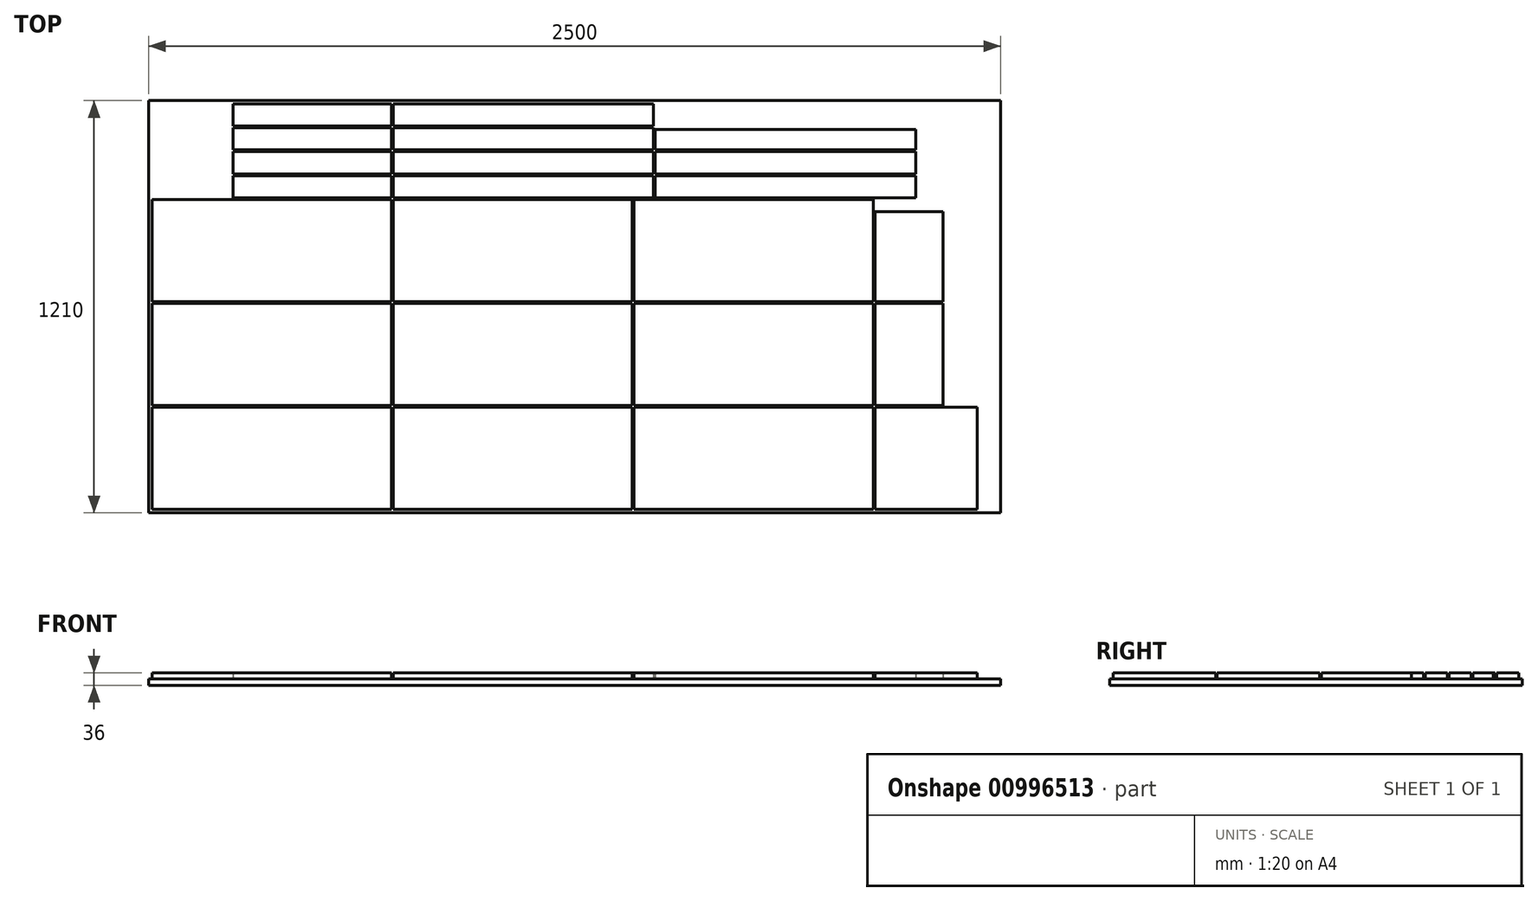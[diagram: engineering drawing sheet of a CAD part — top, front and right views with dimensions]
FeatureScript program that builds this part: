
annotation { "Feature Type Name" : "Feature", "Feature Type Description" : "" }
export const myFeature = defineFeature(function(context is Context, id is Id, definition is map)
    precondition{}
    {
        {
            var Q0;
            Q0=qCreatedBy(makeId("Top.planeOp"),FACE);
            var sketch = newSketch(context, id + "F0", { "sketchPlane" : qUnion([Q0])});
            skLineSegment(sketch, "E0.bottom", {"start": v(0, 0) * mm, "end": v(2500, 0) * mm});
            skLineSegment(sketch, "E0.top", {"start": v(0, 1210) * mm, "end": v(2500, 1210) * mm});
            skLineSegment(sketch, "E0.left", {"start": v(0, 0) * mm, "end": v(0, 1210) * mm});
            skLineSegment(sketch, "E0.right", {"start": v(2500, 0) * mm, "end": v(2500, 1210) * mm});
            skSolve(sketch);
        }
        {
            var Q0;
            Q0=makeQuery(id+"F0.imprint","IMPRINT",FACE,{"disambiguationData":[TD([[makeQuery(id+"F0.imprint","IMPRINT",EDGE,{"derivedFrom":sQuery(id+"F0.wireOp",EDGE,"E0.bottom")}),1.0]])]});
            extrude(context, id + "F1", {"entities" : qUnion([Q0]), "depth" : 18 * mm, "offsetDistance" : 25 * mm});
        }
        {
            var Q0;
            Q0=makeQuery(id+"F1.opExtrude","CAP_FACE",FACE,{"disambiguationData":[OSD([sQuery(id+"F0.wireOp",EDGE,"E0.bottom"),sQuery(id+"F0.wireOp",EDGE,"E0.top"),sQuery(id+"F0.wireOp",EDGE,"E0.left"),sQuery(id+"F0.wireOp",EDGE,"E0.right")])],"isStart":false});
            var sketch = newSketch(context, id + "F2", { "sketchPlane" : qUnion([Q0])});
            skLineSegment(sketch, "E1.bottom", {"start": v(10, 10) * mm, "end": v(712, 10) * mm});
            skLineSegment(sketch, "E1.top", {"start": v(10, 310) * mm, "end": v(712, 310) * mm});
            skLineSegment(sketch, "E1.left", {"start": v(10, 10) * mm, "end": v(10, 310) * mm});
            skLineSegment(sketch, "E1.right", {"start": v(712, 10) * mm, "end": v(712, 310) * mm});
            skLineSegment(sketch, "E2.bottom", {"start": v(717, 10) * mm, "end": v(1419, 10) * mm});
            skLineSegment(sketch, "E2.top", {"start": v(717, 310) * mm, "end": v(1419, 310) * mm});
            skLineSegment(sketch, "E2.left", {"start": v(717, 10) * mm, "end": v(717, 310) * mm});
            skLineSegment(sketch, "E2.right", {"start": v(1419, 10) * mm, "end": v(1419, 310) * mm});
            skLineSegment(sketch, "E3.bottom", {"start": v(10, 315) * mm, "end": v(712, 315) * mm});
            skLineSegment(sketch, "E3.top", {"start": v(10, 615) * mm, "end": v(712, 615) * mm});
            skLineSegment(sketch, "E3.left", {"start": v(10, 315) * mm, "end": v(10, 615) * mm});
            skLineSegment(sketch, "E3.right", {"start": v(712, 315) * mm, "end": v(712, 615) * mm});
            skLineSegment(sketch, "E4.bottom", {"start": v(717, 615) * mm, "end": v(1419, 615) * mm});
            skLineSegment(sketch, "E4.top", {"start": v(717, 315) * mm, "end": v(1419, 315) * mm});
            skLineSegment(sketch, "E4.left", {"start": v(717, 615) * mm, "end": v(717, 315) * mm});
            skLineSegment(sketch, "E4.right", {"start": v(1419, 615) * mm, "end": v(1419, 315) * mm});
            skLineSegment(sketch, "E5.bottom", {"start": v(10, 620) * mm, "end": v(712, 620) * mm});
            skLineSegment(sketch, "E5.top", {"start": v(10, 920) * mm, "end": v(712, 920) * mm});
            skLineSegment(sketch, "E5.left", {"start": v(10, 620) * mm, "end": v(10, 920) * mm});
            skLineSegment(sketch, "E5.right", {"start": v(712, 620) * mm, "end": v(712, 920) * mm});
            skLineSegment(sketch, "E6.bottom", {"start": v(717, 920) * mm, "end": v(1419, 920) * mm});
            skLineSegment(sketch, "E6.top", {"start": v(717, 620) * mm, "end": v(1419, 620) * mm});
            skLineSegment(sketch, "E6.left", {"start": v(717, 920) * mm, "end": v(717, 620) * mm});
            skLineSegment(sketch, "E6.right", {"start": v(1419, 920) * mm, "end": v(1419, 620) * mm});
            skLineSegment(sketch, "E7.bottom", {"start": v(1424, 310) * mm, "end": v(2126, 310) * mm});
            skLineSegment(sketch, "E7.top", {"start": v(1424, 10) * mm, "end": v(2126, 10) * mm});
            skLineSegment(sketch, "E7.left", {"start": v(1424, 310) * mm, "end": v(1424, 10) * mm});
            skLineSegment(sketch, "E7.right", {"start": v(2126, 310) * mm, "end": v(2126, 10) * mm});
            skLineSegment(sketch, "E8.bottom", {"start": v(1424, 615) * mm, "end": v(2126, 615) * mm});
            skLineSegment(sketch, "E8.top", {"start": v(1424, 315) * mm, "end": v(2126, 315) * mm});
            skLineSegment(sketch, "E8.left", {"start": v(1424, 615) * mm, "end": v(1424, 315) * mm});
            skLineSegment(sketch, "E8.right", {"start": v(2126, 615) * mm, "end": v(2126, 315) * mm});
            skLineSegment(sketch, "E9.bottom", {"start": v(1424, 920) * mm, "end": v(2126, 920) * mm});
            skLineSegment(sketch, "E9.top", {"start": v(1424, 620) * mm, "end": v(2126, 620) * mm});
            skLineSegment(sketch, "E9.left", {"start": v(1424, 920) * mm, "end": v(1424, 620) * mm});
            skLineSegment(sketch, "E9.right", {"start": v(2126, 920) * mm, "end": v(2126, 620) * mm});
            skLineSegment(sketch, "E10.bottom", {"start": v(2131, 310) * mm, "end": v(2431, 310) * mm});
            skLineSegment(sketch, "E10.top", {"start": v(2131, 10) * mm, "end": v(2431, 10) * mm});
            skLineSegment(sketch, "E10.left", {"start": v(2131, 310) * mm, "end": v(2131, 10) * mm});
            skLineSegment(sketch, "E10.right", {"start": v(2431, 310) * mm, "end": v(2431, 10) * mm});
            skLineSegment(sketch, "E11.bottom", {"start": v(712, 925) * mm, "end": v(248, 925) * mm});
            skLineSegment(sketch, "E11.top", {"start": v(712, 990) * mm, "end": v(248, 990) * mm});
            skLineSegment(sketch, "E11.left", {"start": v(712, 925) * mm, "end": v(712, 990) * mm});
            skLineSegment(sketch, "E11.right", {"start": v(248, 925) * mm, "end": v(248, 990) * mm});
            skLineSegment(sketch, "E12.bottom", {"start": v(248, 1060) * mm, "end": v(712, 1060) * mm});
            skLineSegment(sketch, "E12.top", {"start": v(248, 995) * mm, "end": v(712, 995) * mm});
            skLineSegment(sketch, "E12.left", {"start": v(248, 1060) * mm, "end": v(248, 995) * mm});
            skLineSegment(sketch, "E12.right", {"start": v(712, 1060) * mm, "end": v(712, 995) * mm});
            skLineSegment(sketch, "E13.bottom", {"start": v(248, 1065) * mm, "end": v(712, 1065) * mm});
            skLineSegment(sketch, "E13.top", {"start": v(248, 1130) * mm, "end": v(712, 1130) * mm});
            skLineSegment(sketch, "E13.left", {"start": v(248, 1065) * mm, "end": v(248, 1130) * mm});
            skLineSegment(sketch, "E13.right", {"start": v(712, 1065) * mm, "end": v(712, 1130) * mm});
            skLineSegment(sketch, "E14.bottom", {"start": v(248, 1135) * mm, "end": v(712, 1135) * mm});
            skLineSegment(sketch, "E14.top", {"start": v(248, 1200) * mm, "end": v(712, 1200) * mm});
            skLineSegment(sketch, "E14.left", {"start": v(248, 1135) * mm, "end": v(248, 1200) * mm});
            skLineSegment(sketch, "E14.right", {"start": v(712, 1135) * mm, "end": v(712, 1200) * mm});
            skLineSegment(sketch, "E15.bottom", {"start": v(2131, 315) * mm, "end": v(2331, 315) * mm});
            skLineSegment(sketch, "E15.top", {"start": v(2131, 615) * mm, "end": v(2331, 615) * mm});
            skLineSegment(sketch, "E15.left", {"start": v(2131, 315) * mm, "end": v(2131, 615) * mm});
            skLineSegment(sketch, "E15.right", {"start": v(2331, 315) * mm, "end": v(2331, 615) * mm});
            skLineSegment(sketch, "E16.bottom", {"start": v(2131, 620) * mm, "end": v(2331, 620) * mm});
            skLineSegment(sketch, "E16.top", {"start": v(2131, 884) * mm, "end": v(2331, 884) * mm});
            skLineSegment(sketch, "E16.left", {"start": v(2131, 620) * mm, "end": v(2131, 884) * mm});
            skLineSegment(sketch, "E16.right", {"start": v(2331, 620) * mm, "end": v(2331, 884) * mm});
            skLineSegment(sketch, "E17.bottom", {"start": v(717, 925) * mm, "end": v(1481, 925) * mm});
            skLineSegment(sketch, "E17.top", {"start": v(717, 990) * mm, "end": v(1481, 990) * mm});
            skLineSegment(sketch, "E17.left", {"start": v(717, 925) * mm, "end": v(717, 990) * mm});
            skLineSegment(sketch, "E17.right", {"start": v(1481, 925) * mm, "end": v(1481, 990) * mm});
            skLineSegment(sketch, "E18.bottom", {"start": v(717, 995) * mm, "end": v(1481, 995) * mm});
            skLineSegment(sketch, "E18.top", {"start": v(717, 1060) * mm, "end": v(1481, 1060) * mm});
            skLineSegment(sketch, "E18.left", {"start": v(717, 995) * mm, "end": v(717, 1060) * mm});
            skLineSegment(sketch, "E18.right", {"start": v(1481, 995) * mm, "end": v(1481, 1060) * mm});
            skLineSegment(sketch, "E19.bottom", {"start": v(717, 1065) * mm, "end": v(1481, 1065) * mm});
            skLineSegment(sketch, "E19.top", {"start": v(717, 1130) * mm, "end": v(1481, 1130) * mm});
            skLineSegment(sketch, "E19.left", {"start": v(717, 1065) * mm, "end": v(717, 1130) * mm});
            skLineSegment(sketch, "E19.right", {"start": v(1481, 1065) * mm, "end": v(1481, 1130) * mm});
            skLineSegment(sketch, "E20.bottom", {"start": v(717, 1135) * mm, "end": v(1481, 1135) * mm});
            skLineSegment(sketch, "E20.top", {"start": v(717, 1200) * mm, "end": v(1481, 1200) * mm});
            skLineSegment(sketch, "E20.left", {"start": v(717, 1135) * mm, "end": v(717, 1200) * mm});
            skLineSegment(sketch, "E20.right", {"start": v(1481, 1135) * mm, "end": v(1481, 1200) * mm});
            skLineSegment(sketch, "E21.bottom", {"start": v(1486, 925) * mm, "end": v(2250, 925) * mm});
            skLineSegment(sketch, "E21.top", {"start": v(1486, 990) * mm, "end": v(2250, 990) * mm});
            skLineSegment(sketch, "E21.left", {"start": v(1486, 925) * mm, "end": v(1486, 990) * mm});
            skLineSegment(sketch, "E21.right", {"start": v(2250, 925) * mm, "end": v(2250, 990) * mm});
            skLineSegment(sketch, "E22.bottom", {"start": v(1486, 1060) * mm, "end": v(2250, 1060) * mm});
            skLineSegment(sketch, "E22.top", {"start": v(1486, 995) * mm, "end": v(2250, 995) * mm});
            skLineSegment(sketch, "E22.left", {"start": v(1486, 1060) * mm, "end": v(1486, 995) * mm});
            skLineSegment(sketch, "E22.right", {"start": v(2250, 1060) * mm, "end": v(2250, 995) * mm});
            skLineSegment(sketch, "E23.bottom", {"start": v(1486, 1125) * mm, "end": v(2250, 1125) * mm});
            skLineSegment(sketch, "E23.top", {"start": v(1486, 1065) * mm, "end": v(2250, 1065) * mm});
            skLineSegment(sketch, "E23.left", {"start": v(1486, 1065) * mm, "end": v(1486, 1125) * mm});
            skLineSegment(sketch, "E23.right", {"start": v(2250, 1065) * mm, "end": v(2250, 1125) * mm});
            skLineSegment(sketch, "E24.bottom", {"start": v(0, 1210) * mm, "end": v(2500, 1210) * mm});
            skLineSegment(sketch, "E24.top", {"start": v(0, 0) * mm, "end": v(2500, 0) * mm});
            skLineSegment(sketch, "E24.left", {"start": v(0, 1210) * mm, "end": v(0, 0) * mm});
            skLineSegment(sketch, "E24.right", {"start": v(2500, 1210) * mm, "end": v(2500, 0) * mm});
            skSolve(sketch);
        }
        {
            var Q0;
            Q0=makeQuery(id+"F2.imprint","IMPRINT",FACE,{"disambiguationData":[TD([[makeQuery(id+"F2.imprint","IMPRINT",EDGE,{"derivedFrom":sQuery(id+"F2.wireOp",EDGE,"E1.bottom")}),1.0]])]});
            var Q1;
            Q1=makeQuery(id+"F2.imprint","IMPRINT",FACE,{"disambiguationData":[TD([[makeQuery(id+"F2.imprint","IMPRINT",EDGE,{"derivedFrom":sQuery(id+"F2.wireOp",EDGE,"E3.bottom")}),1.0]])]});
            var Q2;
            Q2=makeQuery(id+"F2.imprint","IMPRINT",FACE,{"disambiguationData":[TD([[makeQuery(id+"F2.imprint","IMPRINT",EDGE,{"derivedFrom":sQuery(id+"F2.wireOp",EDGE,"E5.bottom")}),1.0]])]});
            var Q3;
            Q3=makeQuery(id+"F2.imprint","IMPRINT",FACE,{"disambiguationData":[TD([[makeQuery(id+"F2.imprint","IMPRINT",EDGE,{"derivedFrom":sQuery(id+"F2.wireOp",EDGE,"E2.bottom")}),1.0]])]});
            var Q4;
            Q4=makeQuery(id+"F2.imprint","IMPRINT",FACE,{"disambiguationData":[TD([[makeQuery(id+"F2.imprint","IMPRINT",EDGE,{"derivedFrom":sQuery(id+"F2.wireOp",EDGE,"E4.bottom")}),-1.0]])]});
            var Q5;
            Q5=makeQuery(id+"F2.imprint","IMPRINT",FACE,{"disambiguationData":[TD([[makeQuery(id+"F2.imprint","IMPRINT",EDGE,{"derivedFrom":sQuery(id+"F2.wireOp",EDGE,"E6.bottom")}),-1.0]])]});
            var Q6;
            Q6=makeQuery(id+"F2.imprint","IMPRINT",FACE,{"disambiguationData":[TD([[makeQuery(id+"F2.imprint","IMPRINT",EDGE,{"derivedFrom":sQuery(id+"F2.wireOp",EDGE,"E11.bottom")}),-1.0]])]});
            var Q7;
            Q7=makeQuery(id+"F2.imprint","IMPRINT",FACE,{"disambiguationData":[TD([[makeQuery(id+"F2.imprint","IMPRINT",EDGE,{"derivedFrom":sQuery(id+"F2.wireOp",EDGE,"E12.bottom")}),-1.0]])]});
            var Q8;
            Q8=makeQuery(id+"F2.imprint","IMPRINT",FACE,{"disambiguationData":[TD([[makeQuery(id+"F2.imprint","IMPRINT",EDGE,{"derivedFrom":sQuery(id+"F2.wireOp",EDGE,"E13.bottom")}),1.0]])]});
            var Q9;
            Q9=makeQuery(id+"F2.imprint","IMPRINT",FACE,{"disambiguationData":[TD([[makeQuery(id+"F2.imprint","IMPRINT",EDGE,{"derivedFrom":sQuery(id+"F2.wireOp",EDGE,"E14.bottom")}),1.0]])]});
            var Q10;
            Q10=makeQuery(id+"F2.imprint","IMPRINT",FACE,{"disambiguationData":[TD([[makeQuery(id+"F2.imprint","IMPRINT",EDGE,{"derivedFrom":sQuery(id+"F2.wireOp",EDGE,"E20.bottom")}),1.0]])]});
            var Q11;
            Q11=makeQuery(id+"F2.imprint","IMPRINT",FACE,{"disambiguationData":[TD([[makeQuery(id+"F2.imprint","IMPRINT",EDGE,{"derivedFrom":sQuery(id+"F2.wireOp",EDGE,"E19.bottom")}),1.0]])]});
            var Q12;
            Q12=makeQuery(id+"F2.imprint","IMPRINT",FACE,{"disambiguationData":[TD([[makeQuery(id+"F2.imprint","IMPRINT",EDGE,{"derivedFrom":sQuery(id+"F2.wireOp",EDGE,"E18.bottom")}),1.0]])]});
            var Q13;
            Q13=makeQuery(id+"F2.imprint","IMPRINT",FACE,{"disambiguationData":[TD([[makeQuery(id+"F2.imprint","IMPRINT",EDGE,{"derivedFrom":sQuery(id+"F2.wireOp",EDGE,"E17.bottom")}),1.0]])]});
            var Q14;
            Q14=makeQuery(id+"F2.imprint","IMPRINT",FACE,{"disambiguationData":[TD([[makeQuery(id+"F2.imprint","IMPRINT",EDGE,{"derivedFrom":sQuery(id+"F2.wireOp",EDGE,"E7.bottom")}),-1.0]])]});
            var Q15;
            Q15=makeQuery(id+"F2.imprint","IMPRINT",FACE,{"disambiguationData":[TD([[makeQuery(id+"F2.imprint","IMPRINT",EDGE,{"derivedFrom":sQuery(id+"F2.wireOp",EDGE,"E8.bottom")}),-1.0]])]});
            var Q16;
            Q16=makeQuery(id+"F2.imprint","IMPRINT",FACE,{"disambiguationData":[TD([[makeQuery(id+"F2.imprint","IMPRINT",EDGE,{"derivedFrom":sQuery(id+"F2.wireOp",EDGE,"E10.bottom")}),-1.0]])]});
            var Q17;
            Q17=makeQuery(id+"F2.imprint","IMPRINT",FACE,{"disambiguationData":[TD([[makeQuery(id+"F2.imprint","IMPRINT",EDGE,{"derivedFrom":sQuery(id+"F2.wireOp",EDGE,"E15.bottom")}),1.0]])]});
            var Q18;
            Q18=makeQuery(id+"F2.imprint","IMPRINT",FACE,{"disambiguationData":[TD([[makeQuery(id+"F2.imprint","IMPRINT",EDGE,{"derivedFrom":sQuery(id+"F2.wireOp",EDGE,"E16.bottom")}),1.0]])]});
            var Q19;
            Q19=makeQuery(id+"F2.imprint","IMPRINT",FACE,{"disambiguationData":[TD([[makeQuery(id+"F2.imprint","IMPRINT",EDGE,{"derivedFrom":sQuery(id+"F2.wireOp",EDGE,"E9.bottom")}),-1.0]])]});
            var Q20;
            Q20=makeQuery(id+"F2.imprint","IMPRINT",FACE,{"disambiguationData":[TD([[makeQuery(id+"F2.imprint","IMPRINT",EDGE,{"derivedFrom":sQuery(id+"F2.wireOp",EDGE,"E21.bottom")}),1.0]])]});
            var Q21;
            Q21=makeQuery(id+"F2.imprint","IMPRINT",FACE,{"disambiguationData":[TD([[makeQuery(id+"F2.imprint","IMPRINT",EDGE,{"derivedFrom":sQuery(id+"F2.wireOp",EDGE,"E22.bottom")}),-1.0]])]});
            var Q22;
            Q22=makeQuery(id+"F2.imprint","IMPRINT",FACE,{"disambiguationData":[TD([[makeQuery(id+"F2.imprint","IMPRINT",EDGE,{"derivedFrom":sQuery(id+"F2.wireOp",EDGE,"E23.bottom")}),-1.0]])]});
            extrude(context, id + "F3", {"entities" : qUnion([Q0, Q1, Q2, Q3, Q4, Q5, Q6, Q7, Q8, Q9, Q10, Q11, Q12, Q13, Q14, Q15, Q16, Q17, Q18, Q19, Q20, Q21, Q22]), "depth" : 18 * mm, "offsetDistance" : 25 * mm});
        }
    });
